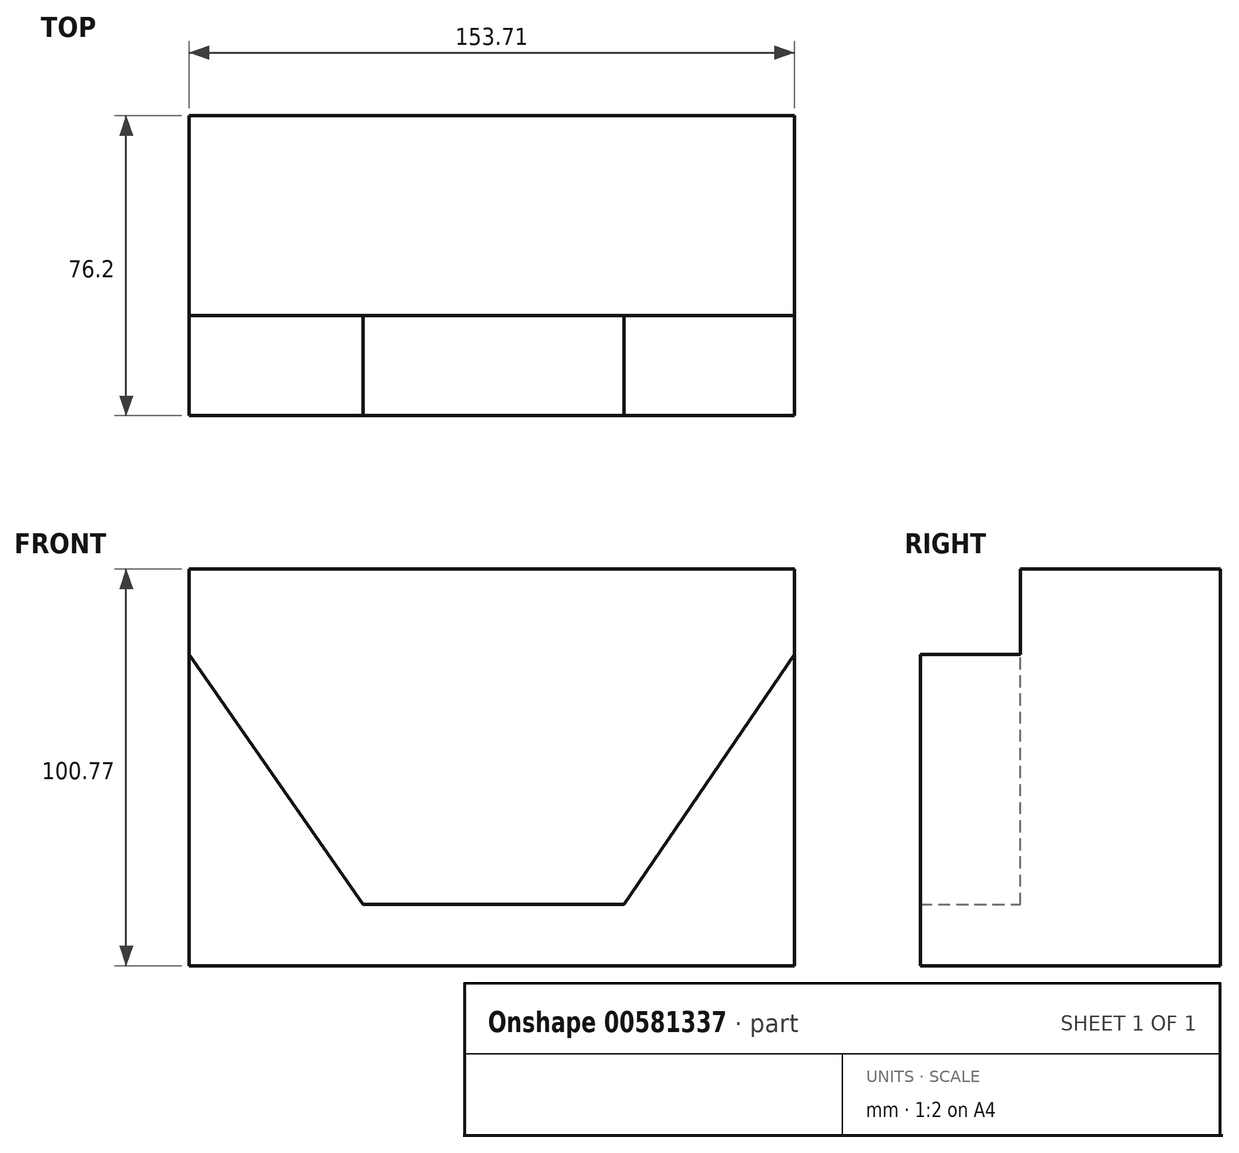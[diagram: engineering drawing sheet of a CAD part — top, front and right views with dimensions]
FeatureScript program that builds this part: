
annotation { "Feature Type Name" : "Feature", "Feature Type Description" : "" }
export const myFeature = defineFeature(function(context is Context, id is Id, definition is map)
    precondition{}
    {
        {
            var Q0;
            Q0=qCreatedBy(makeId("Front.planeOp"),FACE);
            var sketch = newSketch(context, id + "F0", { "sketchPlane" : qUnion([Q0])});
            skLineSegment(sketch, "E0.bottom", {"start": v(-76.61, 56.58) * mm, "end": v(77.1, 56.58) * mm});
            skLineSegment(sketch, "E0.top", {"start": v(-76.61, -44.2) * mm, "end": v(77.1, -44.2) * mm});
            skLineSegment(sketch, "E0.left", {"start": v(-76.61, 56.58) * mm, "end": v(-76.61, -44.2) * mm});
            skLineSegment(sketch, "E0.right", {"start": v(77.1, 56.58) * mm, "end": v(77.1, -44.2) * mm});
            skSolve(sketch);
        }
        {
            var Q0;
            Q0=makeQuery(id+"F0.imprint","IMPRINT",FACE,{"disambiguationData":[TD([[makeQuery(id+"F0.imprint","IMPRINT",EDGE,{"derivedFrom":sQuery(id+"F0.wireOp",EDGE,"E0.bottom")}),-1.0]])]});
            extrude(context, id + "F1", {"entities" : qUnion([Q0]), "depth" : 50.8 * mm, "offsetDistance" : 25.4 * mm});
        }
        {
            var Q0;
            Q0=makeQuery(id+"F1.opExtrude","CAP_FACE",FACE,{"disambiguationData":[OSD([sQuery(id+"F0.wireOp",EDGE,"E0.bottom"),sQuery(id+"F0.wireOp",EDGE,"E0.top"),sQuery(id+"F0.wireOp",EDGE,"E0.left"),sQuery(id+"F0.wireOp",EDGE,"E0.right")])],"isStart":false});
            var sketch = newSketch(context, id + "F2", { "sketchPlane" : qUnion([Q0])});
            skLineSegment(sketch, "E1", {"start": v(-16.4, -28.65) * mm, "end": v(7.16, -28.65) * mm});
            skLineSegment(sketch, "E2", {"start": v(7.16, -28.65) * mm, "end": v(33.87, -28.65) * mm});
            skPoint(sketch, "E3.end.orphan", {"position": v(33.87, -29.62) * mm});
            skPoint(sketch, "E3.start.orphan", {"position": v(77.1, 34.97) * mm});
            skLineSegment(sketch, "E4", {"start": v(33.87, -28.65) * mm, "end": v(77.1, 34.97) * mm});
            skPoint(sketch, "E5.start.orphan", {"position": v(-76.61, 34.97) * mm});
            skLineSegment(sketch, "E6", {"start": v(-16.4, -28.65) * mm, "end": v(-32.4, -28.65) * mm});
            skLineSegment(sketch, "E7", {"start": v(-32.4, -28.65) * mm, "end": v(-76.61, 34.97) * mm});
            skSolve(sketch);
        }
        {
            var Q0;
            Q0=makeQuery(id+"F2.imprint","IMPRINT",FACE,{"disambiguationData":[TD([[makeQuery(id+"F2.imprint","IMPRINT",EDGE,{"derivedFrom":sQuery(id+"F2.wireOp",EDGE,"E1")}),-1.0]])]});
            extrude(context, id + "F3", {"entities" : qUnion([Q0]), "operationType" : NewBodyOperationType.ADD, "depth" : 25.4 * mm, "offsetDistance" : 25.4 * mm});
        }
    });
